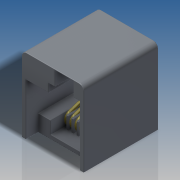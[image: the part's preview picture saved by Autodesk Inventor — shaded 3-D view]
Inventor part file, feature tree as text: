
AUTODESK INVENTOR PART (.ipt)
format: ipt  version: 2016 SP2 (Build 200236200, 236)  size: 381,440 bytes
history: native  units: in
note: dims shown in document units (in); Inventor stores cm internally (conversion verified against a paired STEP export)
features: extrude x7, sketch x4, fillet x2, plane x1, sweep x1, pattern_linear x1
ambient origin geometry x8: Origin, YZ Plane, XZ Plane, XY Plane, X Axis, Y Axis, Z Axis, Center Point
bodies: Solid1 (feature_tree)
feature tree (16):
  sketch  "Sketch2"  dims[d0=0.4724in d1=0.5732in]
  extrude  "Extrusion1"  Depth=0.5732in
  extrude  "Extrusion2"  Depth=0.4094in
  extrude  "Extrusion3"  Depth=0.1417in
  extrude  "Extrusion4"  Depth=0.0787in
  extrude  "Extrusion5"  Depth=0.063in
  extrude  "Extrusion6"  Depth=0.0315in
  sketch  "Sketch3"  dims[d2=0.0378in d3=0.4094in]
  plane  "Work Plane1"
  sweep  "Sweep1"
  pattern_linear  "Rectangular Pattern1"  Spacing1=0.0945in  [1 undecoded]
  extrude  "Extrusion7"  Depth=0.0157in
  fillet  "Fillet1"  Radius=0.2205in
  fillet  "Fillet2"  Radius=0.5669in
  sketch  "Sketch4"  dims[d4=0.0378in d5=0.1417in]
  sketch  "Sketch5"  dims[d6=0.2362in d8=0.0787in d9=0.063in d10=0.0315in d11=0.126in d12=0.0945in d13=0.0157in d14=0.2205in d15=0.5669in d16=0.0in d17=0.5039in d18=0.0in d19=0.1102in d20=0.0in d21=0.378in d22=0.0in d23=0.0945in d24=0.0in d25=0.189in d26=0.0in d27=0.0228in d28=0.0114in d29=0.0394in d31=0.0709in d32=0.0866in d33=0.0in d34=2.3622in d36=0.0394in d37=0.0315in d38=0.1417in d39=0.0in d40=0.0039in d47=0.0039in d48=0.0in]
note: 1 required parameter value undecoded (feature->parameter linkage not recoverable at this tier; creation-order binding heuristic only, values carry confidence <= 0.55)
